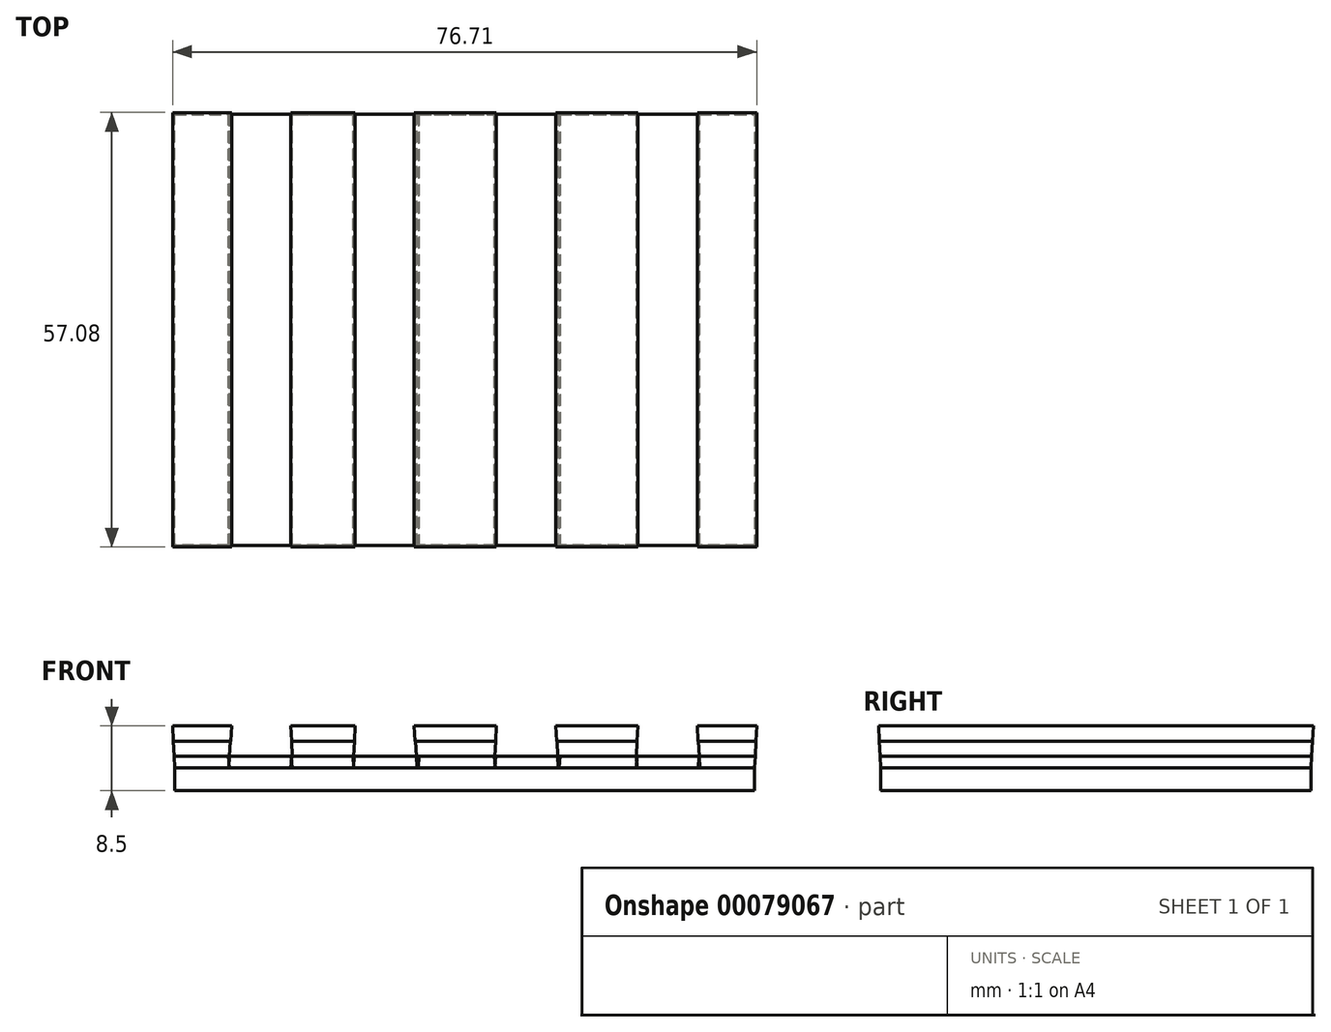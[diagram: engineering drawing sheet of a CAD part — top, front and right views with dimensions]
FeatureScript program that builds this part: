
annotation { "Feature Type Name" : "Feature", "Feature Type Description" : "" }
export const myFeature = defineFeature(function(context is Context, id is Id, definition is map)
    precondition{}
    {
        {
            var Q0;
            Q0=qCreatedBy(makeId("Top.planeOp"),FACE);
            var sketch = newSketch(context, id + "F0", { "sketchPlane" : qUnion([Q0])});
            skLineSegment(sketch, "E0.bottom", {"start": v(-76.14, 56.5) * mm, "end": v(0, 56.5) * mm});
            skLineSegment(sketch, "E0.top", {"start": v(-76.14, 0) * mm, "end": v(0, 0) * mm});
            skLineSegment(sketch, "E0.left", {"start": v(-76.14, 56.5) * mm, "end": v(-76.14, 0) * mm});
            skLineSegment(sketch, "E0.right", {"start": v(0, 56.5) * mm, "end": v(0, 0) * mm});
            skSolve(sketch);
        }
        {
            var Q0;
            Q0=qSketchRegion(id+"F0",true);
            extrude(context, id + "F1", {"entities" : qUnion([Q0]), "depth" : 3 * mm});
        }
        {
            var Q0;
            Q0=makeQuery(id+"F1.opExtrude","CAP_FACE",FACE,{"disambiguationData":[OSD([sQuery(id+"F0.wireOp",EDGE,"E0.bottom"),sQuery(id+"F0.wireOp",EDGE,"E0.top"),sQuery(id+"F0.wireOp",EDGE,"E0.left"),sQuery(id+"F0.wireOp",EDGE,"E0.right")])],"isStart":false});
            var sketch = newSketch(context, id + "F2", { "sketchPlane" : qUnion([Q0])});
            skLineSegment(sketch, "E1.bottom", {"start": v(-76.14, 56.5) * mm, "end": v(0, 56.5) * mm});
            skLineSegment(sketch, "E1.top", {"start": v(-76.14, 0) * mm, "end": v(0, 0) * mm});
            skLineSegment(sketch, "E1.left", {"start": v(-76.14, 56.5) * mm, "end": v(-76.14, 0) * mm});
            skLineSegment(sketch, "E1.right", {"start": v(0, 56.5) * mm, "end": v(0, 0) * mm});
            skSolve(sketch);
        }
        {
            var Q0;
            Q0=makeQuery(id+"F2.imprint","IMPRINT",FACE,{"disambiguationData":[TD([[makeQuery(id+"F2.imprint","IMPRINT",EDGE,{"derivedFrom":sQuery(id+"F2.wireOp",EDGE,"E1.bottom")}),-1.0]])]});
            extrude(context, id + "F3", {"entities" : qUnion([Q0]), "depth" : 1.5 * mm, "hasDraft" : true, "draftAngle" : 3 * degree});
        }
        {
            var Q0;
            Q0=makeQuery(id+"F3.opExtrude","CAP_FACE",FACE,{"disambiguationData":[OSD([sQuery(id+"F2.wireOp",EDGE,"E1.bottom"),sQuery(id+"F2.wireOp",EDGE,"E1.top"),sQuery(id+"F2.wireOp",EDGE,"E1.left"),sQuery(id+"F2.wireOp",EDGE,"E1.right")])],"isStart":false});
            var sketch = newSketch(context, id + "F4", { "sketchPlane" : qUnion([Q0])});
            skLineSegment(sketch, "E2.bottom", {"start": v(-76.22, 56.58) * mm, "end": v(0.08, 56.58) * mm});
            skLineSegment(sketch, "E2.top", {"start": v(-76.22, -0.08) * mm, "end": v(0.08, -0.08) * mm});
            skLineSegment(sketch, "E2.left", {"start": v(-76.22, 56.58) * mm, "end": v(-76.22, -0.08) * mm});
            skLineSegment(sketch, "E2.right", {"start": v(0.08, 56.58) * mm, "end": v(0.08, -0.08) * mm});
            skSolve(sketch);
        }
        {
            var Q0;
            Q0=qSketchRegion(id+"F4",true);
            extrude(context, id + "F5", {"entities" : qUnion([Q0]), "depth" : 2 * mm, "hasDraft" : true, "draftAngle" : 3 * degree});
        }
        {
            var Q0;
            Q0=makeQuery(id+"F5.opExtrude","CAP_FACE",FACE,{"disambiguationData":[OSD([sQuery(id+"F4.wireOp",EDGE,"E2.bottom"),sQuery(id+"F4.wireOp",EDGE,"E2.top"),sQuery(id+"F4.wireOp",EDGE,"E2.left"),sQuery(id+"F4.wireOp",EDGE,"E2.right")])],"isStart":false});
            var sketch = newSketch(context, id + "F6", { "sketchPlane" : qUnion([Q0])});
            skLineSegment(sketch, "E3.bottom", {"start": v(-68.76, 56.68) * mm, "end": v(-60.82, 56.68) * mm});
            skLineSegment(sketch, "E3.top", {"start": v(-68.76, -0.18) * mm, "end": v(-60.82, -0.18) * mm});
            skLineSegment(sketch, "E3.left", {"start": v(-68.76, 56.68) * mm, "end": v(-68.76, -0.18) * mm});
            skLineSegment(sketch, "E3.right", {"start": v(-60.82, 56.68) * mm, "end": v(-60.82, -0.18) * mm});
            skSolve(sketch);
        }
        {
            var Q0;
            Q0=qSketchRegion(id+"F6",true);
            extrude(context, id + "F7", {"entities" : qUnion([Q0]), "operationType" : NewBodyOperationType.REMOVE, "oppositeDirection" : true, "depth" : 2 * mm, "hasDraft" : true, "draftAngle" : 3 * degree});
        }
        {
            var Q0;
            {var subQ0=sQuery(id+"F4.wireOp",EDGE,"E2.bottom");var subQ1=sQuery(id+"F4.wireOp",EDGE,"E2.top");var subQ2=sQuery(id+"F4.wireOp",EDGE,"E2.right");Q0=makeQuery(id+"F7.boolean.opBoolean","SPLIT",FACE,{"disambiguationData":[TD([makeQuery(id+"F5.opExtrude","SWEPT_FACE",FACE,{"disambiguationData":[OSD([subQ2])]})])],"derivedFrom":makeQuery(id+"F5.opExtrude","CAP_FACE",FACE,{"disambiguationData":[OSD([subQ0,subQ1,sQuery(id+"F4.wireOp",EDGE,"E2.left"),subQ2])],"isStart":false})});}
            var sketch = newSketch(context, id + "F8", { "sketchPlane" : qUnion([Q0])});
            skLineSegment(sketch, "E4.bottom", {"start": v(-52.56, 56.68) * mm, "end": v(-44.62, 56.68) * mm});
            skLineSegment(sketch, "E4.top", {"start": v(-52.56, -0.18) * mm, "end": v(-44.62, -0.18) * mm});
            skLineSegment(sketch, "E4.left", {"start": v(-52.56, 56.68) * mm, "end": v(-52.56, -0.18) * mm});
            skLineSegment(sketch, "E4.right", {"start": v(-44.62, 56.68) * mm, "end": v(-44.62, -0.18) * mm});
            skSolve(sketch);
        }
        {
            var Q0;
            Q0=qSketchRegion(id+"F8",true);
            extrude(context, id + "F9", {"entities" : qUnion([Q0]), "operationType" : NewBodyOperationType.REMOVE, "oppositeDirection" : true, "depth" : 2 * mm, "hasDraft" : true, "draftAngle" : 3 * degree});
        }
        {
            var Q0;
            {var subQ0=sQuery(id+"F4.wireOp",EDGE,"E2.bottom");var subQ2=sQuery(id+"F4.wireOp",EDGE,"E2.top");var subQ4=sQuery(id+"F4.wireOp",EDGE,"E2.right");var subQ5=makeQuery(id+"F5.opExtrude","SWEPT_FACE",FACE,{"disambiguationData":[OSD([subQ4])]});Q0=makeQuery(id+"F9.boolean.opBoolean","SPLIT",FACE,{"disambiguationData":[TD([subQ5])],"derivedFrom":makeQuery(id+"F7.boolean.opBoolean","SPLIT",FACE,{"disambiguationData":[TD([subQ5])],"derivedFrom":makeQuery(id+"F5.opExtrude","CAP_FACE",FACE,{"disambiguationData":[OSD([subQ0,subQ2,sQuery(id+"F4.wireOp",EDGE,"E2.left"),subQ4])],"isStart":false})})});}
            var sketch = newSketch(context, id + "F10", { "sketchPlane" : qUnion([Q0])});
            skLineSegment(sketch, "E5.bottom", {"start": v(-34, 56.68) * mm, "end": v(-25.99, 56.68) * mm});
            skLineSegment(sketch, "E5.top", {"start": v(-34, -0.18) * mm, "end": v(-25.99, -0.18) * mm});
            skLineSegment(sketch, "E5.left", {"start": v(-34, 56.68) * mm, "end": v(-34, -0.18) * mm});
            skLineSegment(sketch, "E5.right", {"start": v(-25.99, 56.68) * mm, "end": v(-25.99, -0.18) * mm});
            skSolve(sketch);
        }
        {
            var Q0;
            Q0=qSketchRegion(id+"F10",true);
            extrude(context, id + "F11", {"entities" : qUnion([Q0]), "operationType" : NewBodyOperationType.REMOVE, "oppositeDirection" : true, "depth" : 2 * mm, "hasDraft" : true, "draftAngle" : 3 * degree});
        }
        {
            var Q0;
            {var subQ0=sQuery(id+"F4.wireOp",EDGE,"E2.bottom");var subQ2=sQuery(id+"F4.wireOp",EDGE,"E2.top");var subQ4=sQuery(id+"F4.wireOp",EDGE,"E2.right");var subQ5=makeQuery(id+"F5.opExtrude","SWEPT_FACE",FACE,{"disambiguationData":[OSD([subQ4])]});Q0=makeQuery(id+"F11.boolean.opBoolean","SPLIT",FACE,{"disambiguationData":[TD([subQ5])],"derivedFrom":makeQuery(id+"F9.boolean.opBoolean","SPLIT",FACE,{"disambiguationData":[TD([subQ5])],"derivedFrom":makeQuery(id+"F7.boolean.opBoolean","SPLIT",FACE,{"disambiguationData":[TD([subQ5])],"derivedFrom":makeQuery(id+"F5.opExtrude","CAP_FACE",FACE,{"disambiguationData":[OSD([subQ0,subQ2,sQuery(id+"F4.wireOp",EDGE,"E2.left"),subQ4])],"isStart":false})})})});}
            var sketch = newSketch(context, id + "F12", { "sketchPlane" : qUnion([Q0])});
            skLineSegment(sketch, "E6.bottom", {"start": v(-15.44, 56.68) * mm, "end": v(-7.42, 56.68) * mm});
            skLineSegment(sketch, "E6.top", {"start": v(-15.44, -0.18) * mm, "end": v(-7.42, -0.18) * mm});
            skLineSegment(sketch, "E6.left", {"start": v(-15.44, 56.68) * mm, "end": v(-15.44, -0.18) * mm});
            skLineSegment(sketch, "E6.right", {"start": v(-7.42, 56.68) * mm, "end": v(-7.42, -0.18) * mm});
            skSolve(sketch);
        }
        {
            var Q0;
            Q0=qSketchRegion(id+"F12",true);
            extrude(context, id + "F13", {"entities" : qUnion([Q0]), "operationType" : NewBodyOperationType.REMOVE, "oppositeDirection" : true, "depth" : 2 * mm, "hasDraft" : true, "draftAngle" : 3 * degree});
        }
        {
            var Q0;
            {var subQ0=sQuery(id+"F4.wireOp",EDGE,"E2.bottom");var subQ1=sQuery(id+"F4.wireOp",EDGE,"E2.top");var subQ2=sQuery(id+"F4.wireOp",EDGE,"E2.left");Q0=makeQuery(id+"F7.boolean.opBoolean","SPLIT",FACE,{"disambiguationData":[TD([makeQuery(id+"F5.opExtrude","SWEPT_FACE",FACE,{"disambiguationData":[OSD([subQ2])]})])],"derivedFrom":makeQuery(id+"F5.opExtrude","CAP_FACE",FACE,{"disambiguationData":[OSD([subQ0,subQ1,subQ2,sQuery(id+"F4.wireOp",EDGE,"E2.right")])],"isStart":false})});}
            var sketch = newSketch(context, id + "F14", { "sketchPlane" : qUnion([Q0])});
            skLineSegment(sketch, "E7.bottom", {"start": v(-76.32, 56.68) * mm, "end": v(-68.76, 56.68) * mm});
            skLineSegment(sketch, "E7.top", {"start": v(-76.32, -0.18) * mm, "end": v(-68.76, -0.18) * mm});
            skLineSegment(sketch, "E7.left", {"start": v(-76.32, 56.68) * mm, "end": v(-76.32, -0.18) * mm});
            skLineSegment(sketch, "E7.right", {"start": v(-68.76, 56.68) * mm, "end": v(-68.76, -0.18) * mm});
            skSolve(sketch);
        }
        {
            var Q0;
            Q0=qSketchRegion(id+"F14",true);
            extrude(context, id + "F15", {"entities" : qUnion([Q0]), "depth" : 2 * mm, "hasDraft" : true, "draftAngle" : 3 * degree});
        }
        {
            var Q0;
            {var subQ0=sQuery(id+"F4.wireOp",EDGE,"E2.bottom");var subQ2=sQuery(id+"F4.wireOp",EDGE,"E2.top");var subQ4=makeQuery(id+"F7.opExtrude","SWEPT_FACE",FACE,{"disambiguationData":[OSD([sQuery(id+"F6.wireOp",EDGE,"E3.right")])]});var subQ5=sQuery(id+"F4.wireOp",EDGE,"E2.right");Q0=makeQuery(id+"F9.boolean.opBoolean","SPLIT",FACE,{"disambiguationData":[TD([makeQuery(id+"F7.boolean.opBoolean","COPY",FACE,{"derivedFrom":subQ4})])],"derivedFrom":makeQuery(id+"F7.boolean.opBoolean","SPLIT",FACE,{"disambiguationData":[TD([makeQuery(id+"F5.opExtrude","SWEPT_FACE",FACE,{"disambiguationData":[OSD([subQ5])]})])],"derivedFrom":makeQuery(id+"F5.opExtrude","CAP_FACE",FACE,{"disambiguationData":[OSD([subQ0,subQ2,sQuery(id+"F4.wireOp",EDGE,"E2.left"),subQ5])],"isStart":false})})});}
            var sketch = newSketch(context, id + "F16", { "sketchPlane" : qUnion([Q0])});
            skLineSegment(sketch, "E8.bottom", {"start": v(-60.82, 56.68) * mm, "end": v(-52.56, 56.68) * mm});
            skLineSegment(sketch, "E8.top", {"start": v(-60.82, -0.18) * mm, "end": v(-52.56, -0.18) * mm});
            skLineSegment(sketch, "E8.left", {"start": v(-60.82, 56.68) * mm, "end": v(-60.82, -0.18) * mm});
            skLineSegment(sketch, "E8.right", {"start": v(-52.56, 56.68) * mm, "end": v(-52.56, -0.18) * mm});
            skSolve(sketch);
        }
        {
            var Q0;
            Q0=qSketchRegion(id+"F16",true);
            extrude(context, id + "F17", {"entities" : qUnion([Q0]), "depth" : 2 * mm, "hasDraft" : true, "draftAngle" : 3 * degree});
        }
        {
            var Q0;
            Q0=makeQuery(id+"F3.opExtrude","CAP_FACE",FACE,{"disambiguationData":[OSD([sQuery(id+"F2.wireOp",EDGE,"E1.bottom"),sQuery(id+"F2.wireOp",EDGE,"E1.top"),sQuery(id+"F2.wireOp",EDGE,"E1.left"),sQuery(id+"F2.wireOp",EDGE,"E1.right")])],"isStart":false});
            var sketch = newSketch(context, id + "F18", { "sketchPlane" : qUnion([Q0])});
            skLineSegment(sketch, "E9.bottom", {"start": v(-68.78, 56.58) * mm, "end": v(-61.04, 56.58) * mm});
            skLineSegment(sketch, "E9.top", {"start": v(-68.78, -0.08) * mm, "end": v(-61.04, -0.08) * mm});
            skLineSegment(sketch, "E9.left", {"start": v(-68.78, 56.58) * mm, "end": v(-68.78, -0.08) * mm});
            skLineSegment(sketch, "E9.right", {"start": v(-61.04, 56.58) * mm, "end": v(-61.04, -0.08) * mm});
            skSolve(sketch);
        }
        {
            var Q0;
            Q0=qSketchRegion(id+"F18",true);
            extrude(context, id + "F19", {"entities" : qUnion([Q0]), "depth" : 2 * mm, "hasDraft" : true, "draftAngle" : 3 * degree});
        }
        {
            var Q0;
            Q0=makeQuery(id+"F3.opExtrude","CAP_FACE",FACE,{"disambiguationData":[OSD([sQuery(id+"F2.wireOp",EDGE,"E1.bottom"),sQuery(id+"F2.wireOp",EDGE,"E1.top"),sQuery(id+"F2.wireOp",EDGE,"E1.left"),sQuery(id+"F2.wireOp",EDGE,"E1.right")])],"isStart":false});
            var sketch = newSketch(context, id + "F20", { "sketchPlane" : qUnion([Q0])});
            skLineSegment(sketch, "E10.bottom", {"start": v(-52.37, 56.58) * mm, "end": v(-44.62, 56.58) * mm});
            skLineSegment(sketch, "E10.top", {"start": v(-52.37, -0.08) * mm, "end": v(-44.62, -0.08) * mm});
            skLineSegment(sketch, "E10.left", {"start": v(-52.37, 56.58) * mm, "end": v(-52.37, -0.08) * mm});
            skLineSegment(sketch, "E10.right", {"start": v(-44.62, 56.58) * mm, "end": v(-44.62, -0.08) * mm});
            skSolve(sketch);
        }
        {
            var Q0;
            Q0=qSketchRegion(id+"F20",true);
            extrude(context, id + "F21", {"entities" : qUnion([Q0]), "depth" : 2 * mm, "hasDraft" : true, "draftAngle" : 3 * degree});
        }
        {
            var Q0;
            {var subQ0=sQuery(id+"F4.wireOp",EDGE,"E2.bottom");var subQ2=sQuery(id+"F4.wireOp",EDGE,"E2.top");var subQ4=makeQuery(id+"F9.opExtrude","SWEPT_FACE",FACE,{"disambiguationData":[OSD([sQuery(id+"F8.wireOp",EDGE,"E4.right")])]});var subQ5=sQuery(id+"F4.wireOp",EDGE,"E2.right");var subQ6=makeQuery(id+"F5.opExtrude","SWEPT_FACE",FACE,{"disambiguationData":[OSD([subQ5])]});Q0=makeQuery(id+"F11.boolean.opBoolean","SPLIT",FACE,{"disambiguationData":[TD([makeQuery(id+"F9.boolean.opBoolean","COPY",FACE,{"derivedFrom":subQ4})])],"derivedFrom":makeQuery(id+"F9.boolean.opBoolean","SPLIT",FACE,{"disambiguationData":[TD([subQ6])],"derivedFrom":makeQuery(id+"F7.boolean.opBoolean","SPLIT",FACE,{"disambiguationData":[TD([subQ6])],"derivedFrom":makeQuery(id+"F5.opExtrude","CAP_FACE",FACE,{"disambiguationData":[OSD([subQ0,subQ2,sQuery(id+"F4.wireOp",EDGE,"E2.left"),subQ5])],"isStart":false})})})});}
            var sketch = newSketch(context, id + "F22", { "sketchPlane" : qUnion([Q0])});
            skLineSegment(sketch, "E11.bottom", {"start": v(-44.62, 56.68) * mm, "end": v(-34, 56.68) * mm});
            skLineSegment(sketch, "E11.top", {"start": v(-44.62, -0.18) * mm, "end": v(-34, -0.18) * mm});
            skLineSegment(sketch, "E11.left", {"start": v(-44.62, 56.68) * mm, "end": v(-44.62, -0.18) * mm});
            skLineSegment(sketch, "E11.right", {"start": v(-34, 56.68) * mm, "end": v(-34, -0.18) * mm});
            skSolve(sketch);
        }
        {
            var Q0;
            Q0=qSketchRegion(id+"F22",true);
            extrude(context, id + "F23", {"entities" : qUnion([Q0]), "depth" : 2 * mm, "hasDraft" : true, "draftAngle" : 3 * degree});
        }
        {
            var Q0;
            Q0=makeQuery(id+"F3.opExtrude","CAP_FACE",FACE,{"disambiguationData":[OSD([sQuery(id+"F2.wireOp",EDGE,"E1.bottom"),sQuery(id+"F2.wireOp",EDGE,"E1.top"),sQuery(id+"F2.wireOp",EDGE,"E1.left"),sQuery(id+"F2.wireOp",EDGE,"E1.right")])],"isStart":false});
            var sketch = newSketch(context, id + "F24", { "sketchPlane" : qUnion([Q0])});
            skLineSegment(sketch, "E12.bottom", {"start": v(-33.8, 56.58) * mm, "end": v(-26.06, 56.58) * mm});
            skLineSegment(sketch, "E12.top", {"start": v(-33.8, -0.08) * mm, "end": v(-26.06, -0.08) * mm});
            skLineSegment(sketch, "E12.left", {"start": v(-33.8, 56.58) * mm, "end": v(-33.8, -0.08) * mm});
            skLineSegment(sketch, "E12.right", {"start": v(-26.06, 56.58) * mm, "end": v(-26.06, -0.08) * mm});
            skSolve(sketch);
        }
        {
            var Q0;
            Q0=qSketchRegion(id+"F24",true);
            extrude(context, id + "F25", {"entities" : qUnion([Q0]), "depth" : 2 * mm, "hasDraft" : true, "draftAngle" : 3 * degree});
        }
        {
            var Q0;
            {var subQ0=sQuery(id+"F4.wireOp",EDGE,"E2.bottom");var subQ2=sQuery(id+"F4.wireOp",EDGE,"E2.top");var subQ4=makeQuery(id+"F11.opExtrude","SWEPT_FACE",FACE,{"disambiguationData":[OSD([sQuery(id+"F10.wireOp",EDGE,"E5.right")])]});var subQ5=sQuery(id+"F4.wireOp",EDGE,"E2.right");var subQ6=makeQuery(id+"F5.opExtrude","SWEPT_FACE",FACE,{"disambiguationData":[OSD([subQ5])]});Q0=makeQuery(id+"F13.boolean.opBoolean","SPLIT",FACE,{"disambiguationData":[TD([makeQuery(id+"F11.boolean.opBoolean","COPY",FACE,{"derivedFrom":subQ4})])],"derivedFrom":makeQuery(id+"F11.boolean.opBoolean","SPLIT",FACE,{"disambiguationData":[TD([subQ6])],"derivedFrom":makeQuery(id+"F9.boolean.opBoolean","SPLIT",FACE,{"disambiguationData":[TD([subQ6])],"derivedFrom":makeQuery(id+"F7.boolean.opBoolean","SPLIT",FACE,{"disambiguationData":[TD([subQ6])],"derivedFrom":makeQuery(id+"F5.opExtrude","CAP_FACE",FACE,{"disambiguationData":[OSD([subQ0,subQ2,sQuery(id+"F4.wireOp",EDGE,"E2.left"),subQ5])],"isStart":false})})})})});}
            var sketch = newSketch(context, id + "F26", { "sketchPlane" : qUnion([Q0])});
            skLineSegment(sketch, "E13.bottom", {"start": v(-25.99, 56.68) * mm, "end": v(-15.44, 56.68) * mm});
            skLineSegment(sketch, "E13.top", {"start": v(-25.99, -0.18) * mm, "end": v(-15.44, -0.18) * mm});
            skLineSegment(sketch, "E13.left", {"start": v(-25.99, 56.68) * mm, "end": v(-25.99, -0.18) * mm});
            skLineSegment(sketch, "E13.right", {"start": v(-15.44, 56.68) * mm, "end": v(-15.44, -0.18) * mm});
            skSolve(sketch);
        }
        {
            var Q0;
            Q0=qSketchRegion(id+"F26",true);
            extrude(context, id + "F27", {"entities" : qUnion([Q0]), "depth" : 2 * mm, "hasDraft" : true, "draftAngle" : 3 * degree});
        }
        {
            var Q0;
            Q0=makeQuery(id+"F3.opExtrude","CAP_FACE",FACE,{"disambiguationData":[OSD([sQuery(id+"F2.wireOp",EDGE,"E1.bottom"),sQuery(id+"F2.wireOp",EDGE,"E1.top"),sQuery(id+"F2.wireOp",EDGE,"E1.left"),sQuery(id+"F2.wireOp",EDGE,"E1.right")])],"isStart":false});
            var sketch = newSketch(context, id + "F28", { "sketchPlane" : qUnion([Q0])});
            skLineSegment(sketch, "E14.bottom", {"start": v(-15.24, 56.58) * mm, "end": v(-7.49, 56.58) * mm});
            skLineSegment(sketch, "E14.top", {"start": v(-15.24, -0.08) * mm, "end": v(-7.49, -0.08) * mm});
            skLineSegment(sketch, "E14.left", {"start": v(-15.24, 56.58) * mm, "end": v(-15.24, -0.08) * mm});
            skLineSegment(sketch, "E14.right", {"start": v(-7.49, 56.58) * mm, "end": v(-7.49, -0.08) * mm});
            skSolve(sketch);
        }
        {
            var Q0;
            Q0=qSketchRegion(id+"F28",true);
            extrude(context, id + "F29", {"entities" : qUnion([Q0]), "depth" : 2 * mm, "hasDraft" : true, "draftAngle" : 3 * degree});
        }
        {
            var Q0;
            {var subQ0=sQuery(id+"F4.wireOp",EDGE,"E2.bottom");var subQ2=sQuery(id+"F4.wireOp",EDGE,"E2.top");var subQ4=sQuery(id+"F4.wireOp",EDGE,"E2.right");var subQ5=makeQuery(id+"F5.opExtrude","SWEPT_FACE",FACE,{"disambiguationData":[OSD([subQ4])]});Q0=makeQuery(id+"F13.boolean.opBoolean","SPLIT",FACE,{"disambiguationData":[TD([subQ5])],"derivedFrom":makeQuery(id+"F11.boolean.opBoolean","SPLIT",FACE,{"disambiguationData":[TD([subQ5])],"derivedFrom":makeQuery(id+"F9.boolean.opBoolean","SPLIT",FACE,{"disambiguationData":[TD([subQ5])],"derivedFrom":makeQuery(id+"F7.boolean.opBoolean","SPLIT",FACE,{"disambiguationData":[TD([subQ5])],"derivedFrom":makeQuery(id+"F5.opExtrude","CAP_FACE",FACE,{"disambiguationData":[OSD([subQ0,subQ2,sQuery(id+"F4.wireOp",EDGE,"E2.left"),subQ4])],"isStart":false})})})})});}
            var sketch = newSketch(context, id + "F30", { "sketchPlane" : qUnion([Q0])});
            skLineSegment(sketch, "E15.bottom", {"start": v(-7.42, 56.68) * mm, "end": v(0.18, 56.68) * mm});
            skLineSegment(sketch, "E15.top", {"start": v(-7.42, -0.18) * mm, "end": v(0.18, -0.18) * mm});
            skLineSegment(sketch, "E15.left", {"start": v(-7.42, 56.68) * mm, "end": v(-7.42, -0.18) * mm});
            skLineSegment(sketch, "E15.right", {"start": v(0.18, 56.68) * mm, "end": v(0.18, -0.18) * mm});
            skSolve(sketch);
        }
        {
            var Q0;
            Q0=qSketchRegion(id+"F30",true);
            extrude(context, id + "F31", {"entities" : qUnion([Q0]), "depth" : 2 * mm, "hasDraft" : true, "draftAngle" : 3 * degree});
        }
        {
            var Q0;
            Q0=makeQuery(id+"F19.opExtrude","CAP_FACE",FACE,{"disambiguationData":[OSD([sQuery(id+"F18.wireOp",EDGE,"E9.bottom"),sQuery(id+"F18.wireOp",EDGE,"E9.top"),sQuery(id+"F18.wireOp",EDGE,"E9.left"),sQuery(id+"F18.wireOp",EDGE,"E9.right")])],"isStart":false});
            extrude(context, id + "F32", {"entities" : qUnion([Q0]), "operationType" : NewBodyOperationType.REMOVE, "oppositeDirection" : true, "depth" : 3.5 * mm, "hasDraft" : true, "draftAngle" : 3 * degree});
        }
        {
            var Q0;
            Q0=makeQuery(id+"F21.opExtrude","CAP_FACE",FACE,{"disambiguationData":[OSD([sQuery(id+"F20.wireOp",EDGE,"E10.bottom"),sQuery(id+"F20.wireOp",EDGE,"E10.top"),sQuery(id+"F20.wireOp",EDGE,"E10.left"),sQuery(id+"F20.wireOp",EDGE,"E10.right")])],"isStart":false});
            extrude(context, id + "F33", {"entities" : qUnion([Q0]), "operationType" : NewBodyOperationType.REMOVE, "oppositeDirection" : true, "depth" : 3.5 * mm, "hasDraft" : true, "draftAngle" : 3 * degree});
        }
        {
            var Q0;
            Q0=makeQuery(id+"F25.opExtrude","CAP_FACE",FACE,{"disambiguationData":[OSD([sQuery(id+"F24.wireOp",EDGE,"E12.bottom"),sQuery(id+"F24.wireOp",EDGE,"E12.top"),sQuery(id+"F24.wireOp",EDGE,"E12.left"),sQuery(id+"F24.wireOp",EDGE,"E12.right")])],"isStart":false});
            extrude(context, id + "F34", {"entities" : qUnion([Q0]), "operationType" : NewBodyOperationType.REMOVE, "oppositeDirection" : true, "depth" : 3.5 * mm, "hasDraft" : true, "draftAngle" : 3 * degree});
        }
        {
            var Q0;
            Q0=makeQuery(id+"F29.opExtrude","CAP_FACE",FACE,{"disambiguationData":[OSD([sQuery(id+"F28.wireOp",EDGE,"E14.bottom"),sQuery(id+"F28.wireOp",EDGE,"E14.top"),sQuery(id+"F28.wireOp",EDGE,"E14.left"),sQuery(id+"F28.wireOp",EDGE,"E14.right")])],"isStart":false});
            extrude(context, id + "F35", {"entities" : qUnion([Q0]), "operationType" : NewBodyOperationType.REMOVE, "oppositeDirection" : true, "depth" : 3.5 * mm, "hasDraft" : true, "draftAngle" : 3 * degree});
        }
        {
            var Q0;
            Q0=makeQuery(id+"F1.opExtrude","CAP_FACE",FACE,{"disambiguationData":[OSD([sQuery(id+"F0.wireOp",EDGE,"E0.bottom"),sQuery(id+"F0.wireOp",EDGE,"E0.top"),sQuery(id+"F0.wireOp",EDGE,"E0.left"),sQuery(id+"F0.wireOp",EDGE,"E0.right")])],"isStart":false});
            var sketch = newSketch(context, id + "F36", { "sketchPlane" : qUnion([Q0])});
            skLineSegment(sketch, "E16.bottom", {"start": v(-69.13, 56.5) * mm, "end": v(-60.43, 56.5) * mm});
            skLineSegment(sketch, "E16.top", {"start": v(-69.13, 0) * mm, "end": v(-60.43, 0) * mm});
            skLineSegment(sketch, "E16.left", {"start": v(-69.13, 56.5) * mm, "end": v(-69.13, 0) * mm});
            skLineSegment(sketch, "E16.right", {"start": v(-60.43, 56.5) * mm, "end": v(-60.43, 0) * mm});
            skSolve(sketch);
        }
        {
            var Q0;
            Q0 = qSketchRegion(id + "F36", true);
            extrude(context, id + "F37", {"entities" : qUnion([Q0]), "depth" : 1.5 * mm, "hasDraft" : true, "draftAngle" : 3 * degree});
        }
        {
            var Q0;
            Q0=makeQuery(id+"F1.opExtrude","CAP_FACE",FACE,{"disambiguationData":[OSD([sQuery(id+"F0.wireOp",EDGE,"E0.bottom"),sQuery(id+"F0.wireOp",EDGE,"E0.top"),sQuery(id+"F0.wireOp",EDGE,"E0.left"),sQuery(id+"F0.wireOp",EDGE,"E0.right")])],"isStart":false});
            var sketch = newSketch(context, id + "F38", { "sketchPlane" : qUnion([Q0])});
            skLineSegment(sketch, "E17.bottom", {"start": v(-52.5, 56.5) * mm, "end": v(-44.3, 56.5) * mm});
            skLineSegment(sketch, "E17.top", {"start": v(-52.5, 0) * mm, "end": v(-44.3, 0) * mm});
            skLineSegment(sketch, "E17.left", {"start": v(-52.5, 56.5) * mm, "end": v(-52.5, 0) * mm});
            skLineSegment(sketch, "E17.right", {"start": v(-44.3, 56.5) * mm, "end": v(-44.3, 0) * mm});
            skSolve(sketch);
        }
        {
            var Q0;
            Q0 = qSketchRegion(id + "F38", true);
            extrude(context, id + "F39", {"entities" : qUnion([Q0]), "depth" : 1.5 * mm, "hasDraft" : true, "draftAngle" : 3 * degree});
        }
        {
            var Q0;
            Q0=makeQuery(id+"F37.opExtrude","SWEPT_BODY",BODY,{"disambiguationData":[OSD([sQuery(id+"F36.wireOp",EDGE,"E16.bottom"),sQuery(id+"F36.wireOp",EDGE,"E16.top"),sQuery(id+"F36.wireOp",EDGE,"E16.left"),sQuery(id+"F36.wireOp",EDGE,"E16.right")])]});
            deleteBodies(context, id + "F40", {"entities" : qUnion([Q0])});
        }
        {
            var Q0;
            Q0=makeQuery(id+"F39.opExtrude","SWEPT_BODY",BODY,{"disambiguationData":[OSD([sQuery(id+"F38.wireOp",EDGE,"E17.bottom"),sQuery(id+"F38.wireOp",EDGE,"E17.top"),sQuery(id+"F38.wireOp",EDGE,"E17.left"),sQuery(id+"F38.wireOp",EDGE,"E17.right")])]});
            deleteBodies(context, id + "F41", {"entities" : qUnion([Q0])});
        }
        {
            var Q0;
            Q0=makeQuery(id+"F1.opExtrude","CAP_FACE",FACE,{"disambiguationData":[OSD([sQuery(id+"F0.wireOp",EDGE,"E0.bottom"),sQuery(id+"F0.wireOp",EDGE,"E0.top"),sQuery(id+"F0.wireOp",EDGE,"E0.left"),sQuery(id+"F0.wireOp",EDGE,"E0.right")])],"isStart":false});
            var sketch = newSketch(context, id + "F42", { "sketchPlane" : qUnion([Q0])});
            skLineSegment(sketch, "E18.bottom", {"start": v(-69, 56.5) * mm, "end": v(-60.9, 56.5) * mm});
            skLineSegment(sketch, "E18.top", {"start": v(-69, 0) * mm, "end": v(-60.9, 0) * mm});
            skLineSegment(sketch, "E18.left", {"start": v(-69, 56.5) * mm, "end": v(-69, 0) * mm});
            skLineSegment(sketch, "E18.right", {"start": v(-60.9, 56.5) * mm, "end": v(-60.9, 0) * mm});
            skSolve(sketch);
        }
        {
            var Q0;
            Q0 = qSketchRegion(id + "F42", true);
            extrude(context, id + "F43", {"entities" : qUnion([Q0]), "depth" : 1.5 * mm, "hasDraft" : true, "draftAngle" : 3 * degree});
        }
        {
            var Q0;
            Q0=makeQuery(id+"F1.opExtrude","CAP_FACE",FACE,{"disambiguationData":[OSD([sQuery(id+"F0.wireOp",EDGE,"E0.bottom"),sQuery(id+"F0.wireOp",EDGE,"E0.top"),sQuery(id+"F0.wireOp",EDGE,"E0.left"),sQuery(id+"F0.wireOp",EDGE,"E0.right")])],"isStart":false});
            var sketch = newSketch(context, id + "F44", { "sketchPlane" : qUnion([Q0])});
            skLineSegment(sketch, "E19.bottom", {"start": v(-52.66, 56.5) * mm, "end": v(-44.15, 56.5) * mm});
            skLineSegment(sketch, "E19.top", {"start": v(-52.66, 0) * mm, "end": v(-44.15, 0) * mm});
            skLineSegment(sketch, "E19.left", {"start": v(-52.66, 56.5) * mm, "end": v(-52.66, 0) * mm});
            skLineSegment(sketch, "E19.right", {"start": v(-44.15, 56.5) * mm, "end": v(-44.15, 0) * mm});
            skSolve(sketch);
        }
        {
            var Q0;
            Q0 = qSketchRegion(id + "F44", true);
            extrude(context, id + "F45", {"entities" : qUnion([Q0]), "depth" : 1.5 * mm, "hasDraft" : true, "draftAngle" : 3 * degree});
        }
        {
            var Q0;
            Q0=makeQuery(id+"F1.opExtrude","CAP_FACE",FACE,{"disambiguationData":[OSD([sQuery(id+"F0.wireOp",EDGE,"E0.bottom"),sQuery(id+"F0.wireOp",EDGE,"E0.top"),sQuery(id+"F0.wireOp",EDGE,"E0.left"),sQuery(id+"F0.wireOp",EDGE,"E0.right")])],"isStart":false});
            var sketch = newSketch(context, id + "F46", { "sketchPlane" : qUnion([Q0])});
            skLineSegment(sketch, "E20.bottom", {"start": v(-34.07, 56.5) * mm, "end": v(-25.65, 56.5) * mm});
            skLineSegment(sketch, "E20.top", {"start": v(-34.07, 0) * mm, "end": v(-25.65, 0) * mm});
            skLineSegment(sketch, "E20.left", {"start": v(-34.07, 56.5) * mm, "end": v(-34.07, 0) * mm});
            skLineSegment(sketch, "E20.right", {"start": v(-25.65, 56.5) * mm, "end": v(-25.65, 0) * mm});
            skSolve(sketch);
        }
        {
            var Q0;
            Q0 = qSketchRegion(id + "F46", true);
            extrude(context, id + "F47", {"entities" : qUnion([Q0]), "depth" : 1.5 * mm, "hasDraft" : true, "draftAngle" : 3 * degree});
        }
        {
            var Q0;
            Q0=makeQuery(id+"F1.opExtrude","CAP_FACE",FACE,{"disambiguationData":[OSD([sQuery(id+"F0.wireOp",EDGE,"E0.bottom"),sQuery(id+"F0.wireOp",EDGE,"E0.top"),sQuery(id+"F0.wireOp",EDGE,"E0.left"),sQuery(id+"F0.wireOp",EDGE,"E0.right")])],"isStart":false});
            var sketch = newSketch(context, id + "F48", { "sketchPlane" : qUnion([Q0])});
            skLineSegment(sketch, "E21.bottom", {"start": v(-15.42, 56.5) * mm, "end": v(-7.37, 56.5) * mm});
            skLineSegment(sketch, "E21.top", {"start": v(-15.42, 0) * mm, "end": v(-7.37, 0) * mm});
            skLineSegment(sketch, "E21.left", {"start": v(-15.42, 56.5) * mm, "end": v(-15.42, 0) * mm});
            skLineSegment(sketch, "E21.right", {"start": v(-7.37, 56.5) * mm, "end": v(-7.37, 0) * mm});
            skSolve(sketch);
        }
        {
            var Q0;
            Q0 = qSketchRegion(id + "F48", true);
            extrude(context, id + "F49", {"entities" : qUnion([Q0]), "depth" : 1.5 * mm, "hasDraft" : true, "draftAngle" : 3 * degree});
        }
    });
